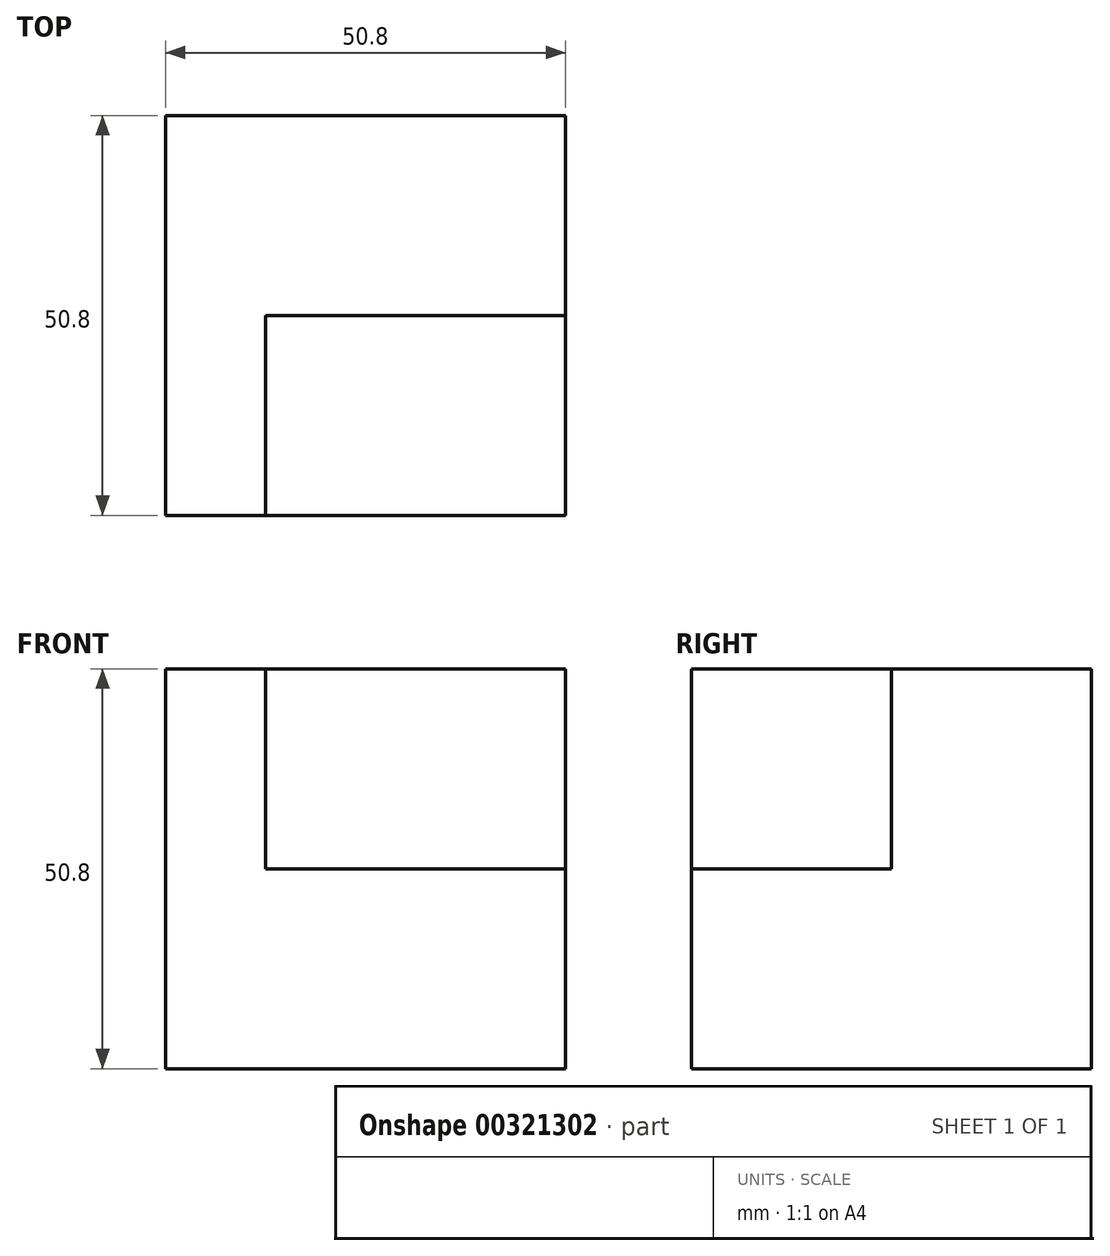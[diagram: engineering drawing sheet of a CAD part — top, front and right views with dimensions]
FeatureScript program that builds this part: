
annotation { "Feature Type Name" : "Feature", "Feature Type Description" : "" }
export const myFeature = defineFeature(function(context is Context, id is Id, definition is map)
    precondition{}
    {
        {
            var Q0;
            Q0=qCreatedBy(makeId("Front.planeOp"),FACE);
            var sketch = newSketch(context, id + "F0", { "sketchPlane" : qUnion([Q0])});
            skLineSegment(sketch, "E0", {"start": v(-42.8, -31.52) * mm, "end": v(8, -31.52) * mm});
            skLineSegment(sketch, "E1", {"start": v(8, -31.52) * mm, "end": v(8, -6.12) * mm});
            skLineSegment(sketch, "E2", {"start": v(8, -6.12) * mm, "end": v(-30.1, -6.12) * mm});
            skLineSegment(sketch, "E3", {"start": v(-30.1, -6.12) * mm, "end": v(-30.1, 19.28) * mm});
            skLineSegment(sketch, "E4", {"start": v(-30.1, 19.28) * mm, "end": v(-42.8, 19.28) * mm});
            skLineSegment(sketch, "E5", {"start": v(-42.8, 19.28) * mm, "end": v(-42.8, -31.52) * mm});
            skLineSegment(sketch, "E6", {"start": v(-30.1, 19.28) * mm, "end": v(8, 19.28) * mm});
            skLineSegment(sketch, "E7", {"start": v(8, 19.28) * mm, "end": v(8, -6.12) * mm});
            skSolve(sketch);
        }
        {
            var Q0;
            Q0 = qSketchRegion(id + "F0", true);
            extrude(context, id + "F1", {"entities" : qUnion([Q0]), "depth" : 50.8 * mm});
        }
        {
            var Q0;
            Q0=makeQuery(id+"F1.opExtrude","SWEPT_FACE",FACE,{"disambiguationData":[OSD([sQuery(id+"F0.wireOp",EDGE,"E4"),sQuery(id+"F0.wireOp",EDGE,"E6")])]});
            var sketch = newSketch(context, id + "F2", { "sketchPlane" : qUnion([Q0])});
            skLineSegment(sketch, "E8", {"start": v(-42.8, -50.8) * mm, "end": v(-30.1, -50.8) * mm});
            skLineSegment(sketch, "E9", {"start": v(-30.1, -50.8) * mm, "end": v(-30.1, -25.4) * mm});
            skLineSegment(sketch, "E10", {"start": v(-30.1, -25.4) * mm, "end": v(8, -25.4) * mm});
            skLineSegment(sketch, "E11", {"start": v(8, -25.4) * mm, "end": v(8, -50.8) * mm});
            skLineSegment(sketch, "E12", {"start": v(8, -50.8) * mm, "end": v(-30.1, -50.8) * mm});
            skSolve(sketch);
        }
        {
            var Q0;
            Q0 = qSketchRegion(id + "F2", true);
            extrude(context, id + "F3", {"entities" : qUnion([Q0]), "operationType" : NewBodyOperationType.REMOVE, "oppositeDirection" : true, "depth" : 25.4 * mm});
        }
    });
